# Revit family: Accessory-Towel_Bar-KOHLER-Strayt-K-9125T
name_source: partatom
category: Specialty Equipment
units: mm (PartAtom-declared; Revit-internal decimal feet)

## family parameters
Cut with Voids When Loaded = No
Host = Face
OmniClass Number = 23.31.25.25
OmniClass Title = Towel Bars
Part Type = Normal
Room Calculation Point = No
Round Connector Dimension = Use Diameter
Shared = No

## types (3) — shared parameters
ADA Compliant = No
Assembly Code = C1030200
Date Modified = 12/06/2022
Default Elevation = 42"
Description = 24 Inch Double Towel Shelf
Finish = Kohler-Metal-CP-Polished_Chrome
Height = 4 3/8"
Length = 25 1/4"
Manufacturer = Kohler Co.
Master Format 2014 = 10 28 00
Master Format 2014 Name = Toilet, Bath, and Laundry Accessories
Material = Premium Metal Construction
Product Name = Strayt
URL = http://www.kohler.com.cn
WaterSense Certified = No
Width = 9 7/16"

## per-type parameters (varying)
| type | Insert | Model | Product Page URL | Secondary Finish | Type |
| CP-Polished Chrome | No | K-9125T-CP | https://www.kohler.com.cn | KOHLER-Plastic-Red | 1 |
| DPR,CP-Polished Chrome | Yes | K-9125T-DPR-CP |  | KOHLER-Plastic-Red | 2 |
| DPW,CP-Polished Chrome | Yes | K-9125T-DPW-CP |  | Kohler-Plastic-0-White | 3 |

## geometry (parser evidence)
native form markers: Sweep x6
no freeform markers — native parametric forms only
